# Revit family: 06.Wichmann Kabelbox BET
name_source: partatom
category: HLS-Bauteile
revit_build: Autodesk Revit 2018 (Build: 20170223_1515(x64)
units: mm (PartAtom-declared; Revit-internal decimal feet)

## family parameters
Basisbauteil = Decke
Beim Laden mit Abzugskörper schneiden = Nein
Bemaßung runder Anschluss = Durchmesser verwenden
Gemeinsam genutzt = Nein
Immer vertikal = Ja
OmniClass-Nummer = 23.75.00.00
OmniClass-Titel = Climate Control (HVAC)
Raumberechnungspunkt = Nein
Teiletyp = Normal

## types (68) — shared parameters
Bautiefe = 270 mm  [stored 0.885827 ft]

## per-type parameters (varying)
| type | BA | BR | Bi | HA | HAN | HR | Hi |
| Kabelbox BET, 110x480x270 mm | 480 mm  [stored 1.5748 ft] | 500 mm  [stored 1.64042 ft] | 450 mm  [stored 1.47638 ft] | 110 mm  [stored 0.360892 ft] | BET110480 | 130 mm  [stored 0.426509 ft] | 70 mm  [stored 0.229659 ft] |
| Kabelbox BET, 110x435x270 mm | 435 mm  [stored 1.42717 ft] | 455 mm | 405 mm | 110 mm  [stored 0.360892 ft] | BET110435 | 130 mm  [stored 0.426509 ft] | 70 mm  [stored 0.229659 ft] |
| Kabelbox BET, 110x335x270 mm | 335 mm  [stored 1.09908 ft] | 355 mm | 305 mm  [stored 1.00066 ft] | 110 mm  [stored 0.360892 ft] | BET110335 | 130 mm  [stored 0.426509 ft] | 70 mm  [stored 0.229659 ft] |
| Kabelbox BET, 110x280x270 mm | 280 mm  [stored 0.918635 ft] | 300 mm | 250 mm  [stored 0.82021 ft] | 110 mm  [stored 0.360892 ft] | BET110280 | 130 mm  [stored 0.426509 ft] | 70 mm  [stored 0.229659 ft] |
| Kabelbox BET, 110x240x270 mm | 240 mm  [stored 0.787402 ft] | 260 mm  [stored 0.853018 ft] | 210 mm  [stored 0.688976 ft] | 110 mm  [stored 0.360892 ft] | BET110240 | 130 mm  [stored 0.426509 ft] | 70 mm  [stored 0.229659 ft] |
| Kabelbox BET, 110x200x270 mm | 200 mm  [stored 0.656168 ft] | 220 mm  [stored 0.721785 ft] | 170 mm  [stored 0.557743 ft] | 110 mm  [stored 0.360892 ft] | BET110200 | 130 mm  [stored 0.426509 ft] | 70 mm  [stored 0.229659 ft] |
| Kabelbox BET, 110x180x270 mm | 180 mm  [stored 0.590551 ft] | 200 mm  [stored 0.656168 ft] | 150 mm | 110 mm  [stored 0.360892 ft] | BET110180 | 130 mm  [stored 0.426509 ft] | 70 mm  [stored 0.229659 ft] |
| Kabelbox BET, 110x160x270 mm | 160 mm  [stored 0.524934 ft] | 180 mm  [stored 0.590551 ft] | 130 mm  [stored 0.426509 ft] | 110 mm  [stored 0.360892 ft] | BET110160 | 130 mm  [stored 0.426509 ft] | 70 mm  [stored 0.229659 ft] |
| Kabelbox BET, 110x120x270 mm | 120 mm  [stored 0.393701 ft] | 140 mm  [stored 0.459318 ft] | 90 mm  [stored 0.295276 ft] | 110 mm  [stored 0.360892 ft] | BET110120 | 130 mm  [stored 0.426509 ft] | 70 mm  [stored 0.229659 ft] |
| Kabelbox BET, 100x640x270 mm | 640 mm | 660 mm | 610 mm | 100 mm  [stored 0.328084 ft] | BET100640 | 120 mm  [stored 0.393701 ft] | 64 mm  [stored 0.209974 ft] |
| Kabelbox BET, 100x580x270 mm | 580 mm | 600 mm | 550 mm | 100 mm  [stored 0.328084 ft] | BET100580 | 120 mm  [stored 0.393701 ft] | 64 mm  [stored 0.209974 ft] |
| Kabelbox BET, 100x535x270 mm | 535 mm  [stored 1.75525 ft] | 555 mm | 505 mm  [stored 1.65682 ft] | 100 mm  [stored 0.328084 ft] | BET100535 | 120 mm  [stored 0.393701 ft] | 64 mm  [stored 0.209974 ft] |
| Kabelbox BET, 100x435x270 mm | 435 mm  [stored 1.42717 ft] | 455 mm | 405 mm | 100 mm  [stored 0.328084 ft] | BET100435 | 120 mm  [stored 0.393701 ft] | 64 mm  [stored 0.209974 ft] |
| Kabelbox BET, 100x380x270 mm | 380 mm | 400 mm  [stored 1.31234 ft] | 350 mm  [stored 1.14829 ft] | 100 mm  [stored 0.328084 ft] | BET100380 | 120 mm  [stored 0.393701 ft] | 64 mm  [stored 0.209974 ft] |
| Kabelbox BET, 100x335x270 mm | 335 mm  [stored 1.09908 ft] | 355 mm | 305 mm  [stored 1.00066 ft] | 100 mm  [stored 0.328084 ft] | BET100335 | 120 mm  [stored 0.393701 ft] | 64 mm  [stored 0.209974 ft] |
| Kabelbox BET, 100x280x270 mm | 280 mm  [stored 0.918635 ft] | 300 mm | 250 mm  [stored 0.82021 ft] | 100 mm  [stored 0.328084 ft] | BET100280 | 120 mm  [stored 0.393701 ft] | 64 mm  [stored 0.209974 ft] |
| Kabelbox BET, 100x240x270 mm | 240 mm  [stored 0.787402 ft] | 260 mm  [stored 0.853018 ft] | 210 mm  [stored 0.688976 ft] | 100 mm  [stored 0.328084 ft] | BET100240 | 120 mm  [stored 0.393701 ft] | 64 mm  [stored 0.209974 ft] |
| Kabelbox BET, 100x200x270 mm | 200 mm  [stored 0.656168 ft] | 220 mm  [stored 0.721785 ft] | 170 mm  [stored 0.557743 ft] | 100 mm  [stored 0.328084 ft] | BET100200 | 120 mm  [stored 0.393701 ft] | 64 mm  [stored 0.209974 ft] |
| Kabelbox BET, 100x180x270 mm | 180 mm  [stored 0.590551 ft] | 200 mm  [stored 0.656168 ft] | 150 mm | 100 mm  [stored 0.328084 ft] | BET100180 | 120 mm  [stored 0.393701 ft] | 64 mm  [stored 0.209974 ft] |
| Kabelbox BET, 100x160x270 mm | 160 mm  [stored 0.524934 ft] | 180 mm  [stored 0.590551 ft] | 130 mm  [stored 0.426509 ft] | 100 mm  [stored 0.328084 ft] | BET100160 | 120 mm  [stored 0.393701 ft] | 64 mm  [stored 0.209974 ft] |
| Kabelbox BET, 100x120x270 mm | 120 mm  [stored 0.393701 ft] | 140 mm  [stored 0.459318 ft] | 90 mm  [stored 0.295276 ft] | 100 mm  [stored 0.328084 ft] | BET100120 | 120 mm  [stored 0.393701 ft] | 64 mm  [stored 0.209974 ft] |
| Kabelbox BET, 90x640x270 mm | 640 mm | 660 mm | 610 mm | 90 mm  [stored 0.295276 ft] | BET090640 | 110 mm  [stored 0.360892 ft] | 56 mm  [stored 0.183727 ft] |
| Kabelbox BET, 90x535x270 mm | 535 mm  [stored 1.75525 ft] | 555 mm | 505 mm  [stored 1.65682 ft] | 90 mm  [stored 0.295276 ft] | BET090535 | 110 mm  [stored 0.360892 ft] | 56 mm  [stored 0.183727 ft] |
| Kabelbox BET, 90x480x270 mm | 480 mm  [stored 1.5748 ft] | 500 mm  [stored 1.64042 ft] | 450 mm  [stored 1.47638 ft] | 90 mm  [stored 0.295276 ft] | BET090480 | 110 mm  [stored 0.360892 ft] | 56 mm  [stored 0.183727 ft] |
| Kabelbox BET, 90x435x270 mm | 435 mm  [stored 1.42717 ft] | 455 mm | 405 mm | 90 mm  [stored 0.295276 ft] | BET090435 | 110 mm  [stored 0.360892 ft] | 56 mm  [stored 0.183727 ft] |
| Kabelbox BET, 90x380x270 mm | 380 mm | 400 mm  [stored 1.31234 ft] | 350 mm  [stored 1.14829 ft] | 90 mm  [stored 0.295276 ft] | BET090380 | 110 mm  [stored 0.360892 ft] | 56 mm  [stored 0.183727 ft] |
| Kabelbox BET, 90x335x270 mm | 335 mm  [stored 1.09908 ft] | 355 mm | 305 mm  [stored 1.00066 ft] | 90 mm  [stored 0.295276 ft] | BET090335 | 110 mm  [stored 0.360892 ft] | 56 mm  [stored 0.183727 ft] |
| Kabelbox BET, 90x280x270 mm | 280 mm  [stored 0.918635 ft] | 300 mm | 250 mm  [stored 0.82021 ft] | 90 mm  [stored 0.295276 ft] | BET090280 | 110 mm  [stored 0.360892 ft] | 56 mm  [stored 0.183727 ft] |
| Kabelbox BET, 90x240x270 mm | 240 mm  [stored 0.787402 ft] | 260 mm  [stored 0.853018 ft] | 210 mm  [stored 0.688976 ft] | 90 mm  [stored 0.295276 ft] | BET090240 | 110 mm  [stored 0.360892 ft] | 56 mm  [stored 0.183727 ft] |
| Kabelbox BET, 90x200x270 mm | 200 mm  [stored 0.656168 ft] | 220 mm  [stored 0.721785 ft] | 170 mm  [stored 0.557743 ft] | 90 mm  [stored 0.295276 ft] | BET090200 | 110 mm  [stored 0.360892 ft] | 56 mm  [stored 0.183727 ft] |
| Kabelbox BET, 90x180x270 mm | 180 mm  [stored 0.590551 ft] | 200 mm  [stored 0.656168 ft] | 150 mm | 90 mm  [stored 0.295276 ft] | BET090180 | 110 mm  [stored 0.360892 ft] | 56 mm  [stored 0.183727 ft] |
| Kabelbox BET, 90x160x270 mm | 160 mm  [stored 0.524934 ft] | 180 mm  [stored 0.590551 ft] | 130 mm  [stored 0.426509 ft] | 90 mm  [stored 0.295276 ft] | BET090160 | 110 mm  [stored 0.360892 ft] | 56 mm  [stored 0.183727 ft] |
| Kabelbox BET, 90x90x270 mm | 90 mm  [stored 0.295276 ft] | 110 mm  [stored 0.360892 ft] | 60 mm  [stored 0.19685 ft] | 90 mm  [stored 0.295276 ft] | BET090090 | 110 mm  [stored 0.360892 ft] | 56 mm  [stored 0.183727 ft] |
| Kabelbox BET, 80x640x270 mm | 640 mm | 660 mm | 610 mm | 80 mm  [stored 0.262467 ft] | BET080640 | 100 mm  [stored 0.328084 ft] | 50 mm  [stored 0.164042 ft] |
| Kabelbox BET, 80x580x270 mm | 580 mm | 600 mm | 550 mm | 80 mm  [stored 0.262467 ft] | BET080580 | 100 mm  [stored 0.328084 ft] | 50 mm  [stored 0.164042 ft] |
| Kabelbox BET, 80x535x270 mm | 535 mm  [stored 1.75525 ft] | 555 mm | 505 mm  [stored 1.65682 ft] | 80 mm  [stored 0.262467 ft] | BET080535 | 100 mm  [stored 0.328084 ft] | 50 mm  [stored 0.164042 ft] |
| Kabelbox BET, 80x480x270 mm | 480 mm  [stored 1.5748 ft] | 500 mm  [stored 1.64042 ft] | 450 mm  [stored 1.47638 ft] | 80 mm  [stored 0.262467 ft] | BET080480 | 100 mm  [stored 0.328084 ft] | 50 mm  [stored 0.164042 ft] |
| Kabelbox BET, 80x435x270 mm | 435 mm  [stored 1.42717 ft] | 455 mm | 405 mm | 80 mm  [stored 0.262467 ft] | BET080435 | 100 mm  [stored 0.328084 ft] | 50 mm  [stored 0.164042 ft] |
| Kabelbox BET, 80x380x270 mm | 380 mm | 400 mm  [stored 1.31234 ft] | 350 mm  [stored 1.14829 ft] | 80 mm  [stored 0.262467 ft] | BET080380 | 100 mm  [stored 0.328084 ft] | 50 mm  [stored 0.164042 ft] |
| Kabelbox BET, 80x335x270 mm | 335 mm  [stored 1.09908 ft] | 355 mm | 305 mm  [stored 1.00066 ft] | 80 mm  [stored 0.262467 ft] | BET080335 | 100 mm  [stored 0.328084 ft] | 50 mm  [stored 0.164042 ft] |
| Kabelbox BET, 80x280x270 mm | 280 mm  [stored 0.918635 ft] | 300 mm | 250 mm  [stored 0.82021 ft] | 80 mm  [stored 0.262467 ft] | BET080280 | 100 mm  [stored 0.328084 ft] | 50 mm  [stored 0.164042 ft] |
| Kabelbox BET, 80x240x270 mm | 240 mm  [stored 0.787402 ft] | 260 mm  [stored 0.853018 ft] | 210 mm  [stored 0.688976 ft] | 80 mm  [stored 0.262467 ft] | BET080240 | 100 mm  [stored 0.328084 ft] | 50 mm  [stored 0.164042 ft] |
| Kabelbox BET, 80x180x270 mm | 180 mm  [stored 0.590551 ft] | 200 mm  [stored 0.656168 ft] | 150 mm | 80 mm  [stored 0.262467 ft] | BET080180 | 100 mm  [stored 0.328084 ft] | 50 mm  [stored 0.164042 ft] |
| Kabelbox BET, 80x160x270 mm | 160 mm  [stored 0.524934 ft] | 180 mm  [stored 0.590551 ft] | 130 mm  [stored 0.426509 ft] | 80 mm  [stored 0.262467 ft] | BET080160 | 100 mm  [stored 0.328084 ft] | 50 mm  [stored 0.164042 ft] |
| Kabelbox BET, 80x120x270 mm | 120 mm  [stored 0.393701 ft] | 140 mm  [stored 0.459318 ft] | 90 mm  [stored 0.295276 ft] | 80 mm  [stored 0.262467 ft] | BET080120 | 100 mm  [stored 0.328084 ft] | 50 mm  [stored 0.164042 ft] |
| Kabelbox BET, 80x90x270 mm | 90 mm  [stored 0.295276 ft] | 110 mm  [stored 0.360892 ft] | 60 mm  [stored 0.19685 ft] | 80 mm  [stored 0.262467 ft] | BET080090 | 100 mm  [stored 0.328084 ft] | 50 mm  [stored 0.164042 ft] |
| Kabelbox BET, 60x640x270 mm | 640 mm | 660 mm | 610 mm | 60 mm  [stored 0.19685 ft] | BET060640 | 80 mm  [stored 0.262467 ft] | 33 mm  [stored 0.108268 ft] |
| Kabelbox BET, 60x580x270 mm | 580 mm | 600 mm | 550 mm | 60 mm  [stored 0.19685 ft] | BET060580 | 80 mm  [stored 0.262467 ft] | 33 mm  [stored 0.108268 ft] |
| Kabelbox BET, 60x535x270 mm | 535 mm  [stored 1.75525 ft] | 555 mm | 505 mm  [stored 1.65682 ft] | 60 mm  [stored 0.19685 ft] | BET060535 | 80 mm  [stored 0.262467 ft] | 33 mm  [stored 0.108268 ft] |
| Kabelbox BET, 60x480x270 mm | 480 mm  [stored 1.5748 ft] | 500 mm  [stored 1.64042 ft] | 450 mm  [stored 1.47638 ft] | 60 mm  [stored 0.19685 ft] | BET060480 | 80 mm  [stored 0.262467 ft] | 33 mm  [stored 0.108268 ft] |
| Kabelbox BET, 60x435x270 mm | 435 mm  [stored 1.42717 ft] | 455 mm | 405 mm | 60 mm  [stored 0.19685 ft] | BET060435 | 80 mm  [stored 0.262467 ft] | 33 mm  [stored 0.108268 ft] |
| Kabelbox BET, 60x380x270 mm | 380 mm | 400 mm  [stored 1.31234 ft] | 350 mm  [stored 1.14829 ft] | 60 mm  [stored 0.19685 ft] | BET060380 | 80 mm  [stored 0.262467 ft] | 33 mm  [stored 0.108268 ft] |
| Kabelbox BET, 60x280x270 mm | 280 mm  [stored 0.918635 ft] | 300 mm | 250 mm  [stored 0.82021 ft] | 60 mm  [stored 0.19685 ft] | BET060280 | 80 mm  [stored 0.262467 ft] | 33 mm  [stored 0.108268 ft] |
| Kabelbox BET, 60x240x270 mm | 240 mm  [stored 0.787402 ft] | 260 mm  [stored 0.853018 ft] | 210 mm  [stored 0.688976 ft] | 60 mm  [stored 0.19685 ft] | BET060240 | 80 mm  [stored 0.262467 ft] | 33 mm  [stored 0.108268 ft] |
| Kabelbox BET, 60x200x270 mm | 200 mm  [stored 0.656168 ft] | 220 mm  [stored 0.721785 ft] | 170 mm  [stored 0.557743 ft] | 60 mm  [stored 0.19685 ft] | BET060200 | 80 mm  [stored 0.262467 ft] | 33 mm  [stored 0.108268 ft] |
| Kabelbox BET, 60x180x270 mm | 180 mm  [stored 0.590551 ft] | 200 mm  [stored 0.656168 ft] | 150 mm | 60 mm  [stored 0.19685 ft] | BET060180 | 80 mm  [stored 0.262467 ft] | 33 mm  [stored 0.108268 ft] |
| Kabelbox BET, 60x160x270 mm | 160 mm  [stored 0.524934 ft] | 180 mm  [stored 0.590551 ft] | 130 mm  [stored 0.426509 ft] | 60 mm  [stored 0.19685 ft] | BET060160 | 80 mm  [stored 0.262467 ft] | 33 mm  [stored 0.108268 ft] |
| Kabelbox BET, 60x120x270 mm | 120 mm  [stored 0.393701 ft] | 140 mm  [stored 0.459318 ft] | 90 mm  [stored 0.295276 ft] | 60 mm  [stored 0.19685 ft] | BET060120 | 80 mm  [stored 0.262467 ft] | 33 mm  [stored 0.108268 ft] |
| Kabelbox BET, 60x90x270 mm | 90 mm  [stored 0.295276 ft] | 110 mm  [stored 0.360892 ft] | 60 mm  [stored 0.19685 ft] | 60 mm  [stored 0.19685 ft] | BET060090 | 80 mm  [stored 0.262467 ft] | 33 mm  [stored 0.108268 ft] |
| Kabelbox BET, 110x640x270 mm | 640 mm | 660 mm | 610 mm | 110 mm  [stored 0.360892 ft] | BET110640 | 130 mm  [stored 0.426509 ft] | 70 mm  [stored 0.229659 ft] |
| Kabelbox BET, 110x580x270 mm | 580 mm | 600 mm | 550 mm | 110 mm  [stored 0.360892 ft] | BET110580 | 130 mm  [stored 0.426509 ft] | 70 mm  [stored 0.229659 ft] |
| Kabelbox BET, 110x535x270 mm | 535 mm  [stored 1.75525 ft] | 555 mm | 505 mm  [stored 1.65682 ft] | 110 mm  [stored 0.360892 ft] | BET110535 | 130 mm  [stored 0.426509 ft] | 70 mm  [stored 0.229659 ft] |
| Kabelbox BET, 110x380x270 mm | 380 mm | 400 mm  [stored 1.31234 ft] | 350 mm  [stored 1.14829 ft] | 110 mm  [stored 0.360892 ft] | BET110380 | 130 mm  [stored 0.426509 ft] | 70 mm  [stored 0.229659 ft] |
| Kabelbox BET, 100x480x270 mm | 480 mm  [stored 1.5748 ft] | 500 mm  [stored 1.64042 ft] | 450 mm  [stored 1.47638 ft] | 100 mm  [stored 0.328084 ft] | BET100480 | 120 mm  [stored 0.393701 ft] | 64 mm  [stored 0.209974 ft] |
| Kabelbox BET, 90x580x270 mm | 580 mm | 600 mm | 550 mm | 90 mm  [stored 0.295276 ft] | BET090580 | 110 mm  [stored 0.360892 ft] | 56 mm  [stored 0.183727 ft] |
| Kabelbox BET, 90x120x270 mm | 120 mm  [stored 0.393701 ft] | 140 mm  [stored 0.459318 ft] | 90 mm  [stored 0.295276 ft] | 90 mm  [stored 0.295276 ft] | BET090120 | 110 mm  [stored 0.360892 ft] | 56 mm  [stored 0.183727 ft] |
| Kabelbox BET, 80x200x270 mm | 200 mm  [stored 0.656168 ft] | 220 mm  [stored 0.721785 ft] | 170 mm  [stored 0.557743 ft] | 80 mm  [stored 0.262467 ft] | BET080200 | 100 mm  [stored 0.328084 ft] | 50 mm  [stored 0.164042 ft] |
| Kabelbox BET, 60x335x270 mm | 335 mm  [stored 1.09908 ft] | 355 mm | 305 mm  [stored 1.00066 ft] | 60 mm  [stored 0.19685 ft] | BET060335 | 80 mm  [stored 0.262467 ft] | 33 mm  [stored 0.108268 ft] |

note: [stored X ft] marks values corroborated as IEEE doubles in the binary element streams (Revit-internal decimal feet)

## geometry (parser evidence)
native form markers: Sweep x2
no freeform markers — native parametric forms only
